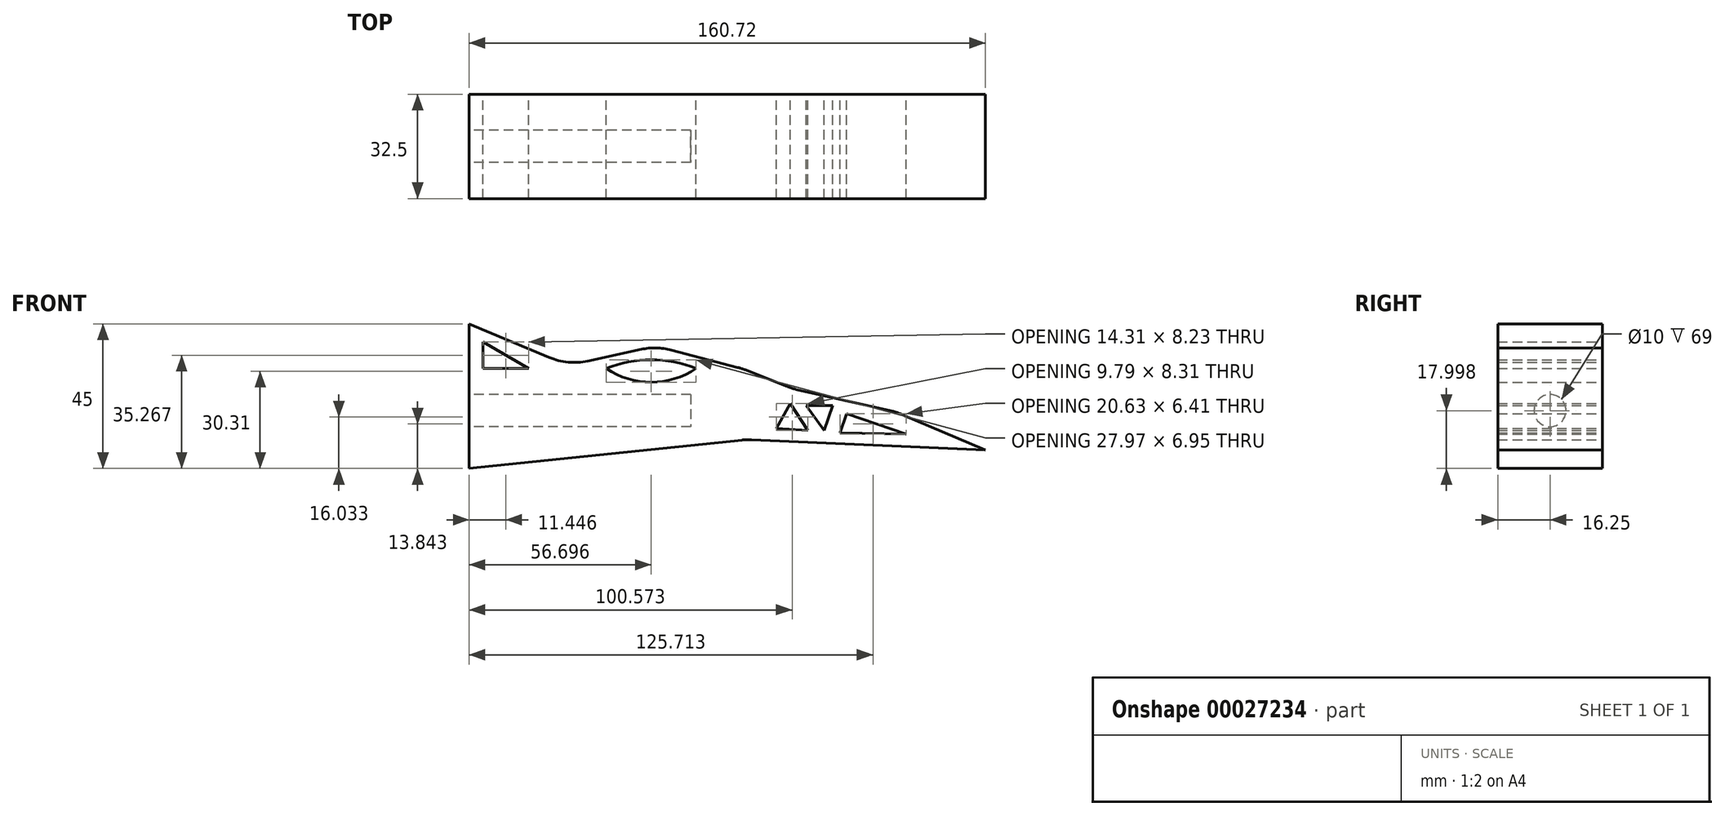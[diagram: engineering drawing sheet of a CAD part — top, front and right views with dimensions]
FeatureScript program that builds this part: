
annotation { "Feature Type Name" : "Feature", "Feature Type Description" : "" }
export const myFeature = defineFeature(function(context is Context, id is Id, definition is map)
    precondition{}
    {
        {
            var Q0;
            Q0=qCreatedBy(makeId("Front.planeOp"),FACE);
            var sketch = newSketch(context, id + "F0", { "sketchPlane" : qUnion([Q0])});
            skLineSegment(sketch, "E0", {"start": v(-70.68, 13.85) * mm, "end": v(-70.68, -31.15) * mm});
            skLineSegment(sketch, "E1", {"start": v(-70.68, 13.85) * mm, "end": v(-45.74, 3.4) * mm});
            skLineSegment(sketch, "E2", {"start": v(-33.75, 2.3) * mm, "end": v(-17.1, 5.93) * mm});
            skLineSegment(sketch, "E3", {"start": v(-7.78, 5.73) * mm, "end": v(12.9, 0.3) * mm});
            skLineSegment(sketch, "E4", {"start": v(15.2, -0.45) * mm, "end": v(28.27, -5.64) * mm});
            skLineSegment(sketch, "E5", {"start": v(31.21, -6.55) * mm, "end": v(60.63, -13.24) * mm});
            skLineSegment(sketch, "E6", {"start": v(64, -14.33) * mm, "end": v(90.04, -25.37) * mm});
            skLineSegment(sketch, "E7", {"start": v(90.04, -25.37) * mm, "end": v(17.2, -22.2) * mm});
            skLineSegment(sketch, "E8", {"start": v(14.27, -22.3) * mm, "end": v(-70.68, -31.15) * mm});
            skPoint(sketch, "E9.visualSharp", {"position": v(-39.92, 0.96) * mm});
            skArc(sketch, "E9.filletArc", {"start": v(-45.74, 3.4) * mm, "mid": v(-39.83, 1.93) * mm, "end": v(-33.75, 2.3) * mm});
            skPoint(sketch, "E10.visualSharp", {"position": v(-12.42, 6.95) * mm});
            skArc(sketch, "E10.filletArc", {"start": v(-7.78, 5.73) * mm, "mid": v(-12.43, 6.38) * mm, "end": v(-17.1, 5.93) * mm});
            skPoint(sketch, "E11.visualSharp", {"position": v(14.08, 0) * mm});
            skArc(sketch, "E11.filletArc", {"start": v(15.2, -0.45) * mm, "mid": v(14.07, -0.04) * mm, "end": v(12.9, 0.3) * mm});
            skPoint(sketch, "E12.visualSharp", {"position": v(29.7, -6.2) * mm});
            skArc(sketch, "E12.filletArc", {"start": v(28.27, -5.64) * mm, "mid": v(29.72, -6.15) * mm, "end": v(31.21, -6.55) * mm});
            skPoint(sketch, "E13.visualSharp", {"position": v(62.37, -13.64) * mm});
            skArc(sketch, "E13.filletArc", {"start": v(64, -14.33) * mm, "mid": v(62.34, -13.71) * mm, "end": v(60.63, -13.24) * mm});
            skPoint(sketch, "E14.visualSharp", {"position": v(15.73, -22.14) * mm});
            skArc(sketch, "E14.filletArc", {"start": v(17.2, -22.2) * mm, "mid": v(15.73, -22.2) * mm, "end": v(14.27, -22.3) * mm});
            skLineSegment(sketch, "E15", {"start": v(-66.39, 8.23) * mm, "end": v(-66.39, 0) * mm});
            skLineSegment(sketch, "E16", {"start": v(-66.39, 0) * mm, "end": v(-52.08, 0) * mm});
            skLineSegment(sketch, "E17", {"start": v(-66.39, 8.23) * mm, "end": v(-52.08, 0) * mm});
            skLineSegment(sketch, "E18", {"start": v(29.25, -10.96) * mm, "end": v(25, -18.72) * mm});
            skLineSegment(sketch, "E19", {"start": v(29.25, -10.96) * mm, "end": v(34.79, -19.27) * mm});
            skLineSegment(sketch, "E20", {"start": v(25, -18.72) * mm, "end": v(34.79, -19.27) * mm});
            skLineSegment(sketch, "E21", {"start": v(34.25, -11.51) * mm, "end": v(39.79, -19.27) * mm});
            skLineSegment(sketch, "E22", {"start": v(34.25, -11.51) * mm, "end": v(42.52, -11.51) * mm});
            skLineSegment(sketch, "E23", {"start": v(42.52, -11.51) * mm, "end": v(39.79, -19.27) * mm});
            skLineSegment(sketch, "E24", {"start": v(46.8, -14.1) * mm, "end": v(44.72, -20.13) * mm});
            skLineSegment(sketch, "E25", {"start": v(46.8, -14.1) * mm, "end": v(65.35, -20.51) * mm});
            skLineSegment(sketch, "E26", {"start": v(44.72, -20.13) * mm, "end": v(65.35, -20.51) * mm});
            skArc(sketch, "E27", {"start": v(0, 0) * mm, "mid": v(-13.98, 2.64) * mm, "end": v(-27.97, 0) * mm});
            skArc(sketch, "E28", {"start": v(-27.97, 0) * mm, "mid": v(-13.98, -4.32) * mm, "end": v(0, 0) * mm});
            skSolve(sketch);
        }
        {
            var Q0;
            Q0=makeQuery(id+"F0.imprint","IMPRINT",FACE,{"disambiguationData":[TD([[makeQuery(id+"F0.imprint","IMPRINT",EDGE,{"derivedFrom":sQuery(id+"F0.wireOp",EDGE,"E0")}),1.0]])]});
            extrude(context, id + "F1", {"entities" : qUnion([Q0]), "depth" : 32.5 * mm});
        }
        {
            var Q0;
            Q0=makeQuery(id+"F1.opExtrude","SWEPT_FACE",FACE,{"disambiguationData":[OSD([sQuery(id+"F0.wireOp",EDGE,"E0")])]});
            var sketch = newSketch(context, id + "F2", { "sketchPlane" : qUnion([Q0])});
            skCircle(sketch, "E29", {"center": v(16.25, -13.15) * mm, "radius": 5 * mm});
            skSolve(sketch);
        }
        {
            var Q0;
            Q0=makeQuery(id+"F2.imprint","IMPRINT",FACE,{"disambiguationData":[TD([[makeQuery(id+"F2.imprint","IMPRINT",EDGE,{"derivedFrom":sQuery(id+"F2.wireOp",EDGE,"E29")}),1.0]])]});
            extrude(context, id + "F3", {"entities" : qUnion([Q0]), "operationType" : NewBodyOperationType.REMOVE, "oppositeDirection" : true, "depth" : 69 * mm});
        }
        {
            var Q0;
            Q0=makeQuery(id+"F0.imprint","IMPRINT",FACE,{"disambiguationData":[TD([[makeQuery(id+"F0.imprint","IMPRINT",EDGE,{"derivedFrom":sQuery(id+"F0.wireOp",EDGE,"E15")}),1.0]])]});
            extrude(context, id + "F4", {"entities" : qUnion([Q0]), "operationType" : NewBodyOperationType.REMOVE, "endBound" : BoundingType.THROUGH_ALL, "oppositeDirection" : true, "depth" : 25 * mm});
        }
    });
